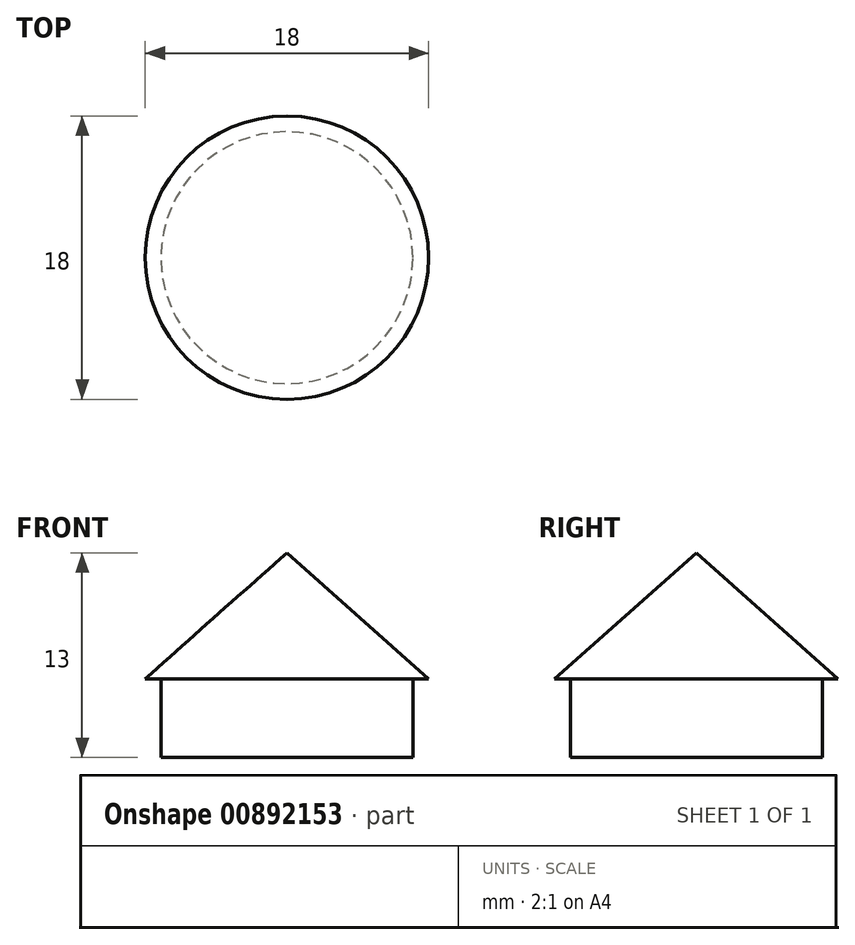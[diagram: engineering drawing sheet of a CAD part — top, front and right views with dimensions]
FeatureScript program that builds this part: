
annotation { "Feature Type Name" : "Feature", "Feature Type Description" : "" }
export const myFeature = defineFeature(function(context is Context, id is Id, definition is map)
    precondition{}
    {
        {
            var Q0;
            Q0=qCreatedBy(makeId("Top.planeOp"),FACE);
            var sketch = newSketch(context, id + "F0", { "sketchPlane" : qUnion([Q0])});
            skCircle(sketch, "E0", {"center": v(0, 0) * mm, "radius": 8 * mm});
            skSolve(sketch);
        }
        {
            var Q0;
            Q0 = qSketchRegion(id + "F0", true);
            extrude(context, id + "F1", {"entities" : qUnion([Q0]), "oppositeDirection" : true, "depth" : 5 * mm, "offsetDistance" : 25 * mm});
        }
        {
            var Q0;
            Q0=qCreatedBy(makeId("Right.planeOp"),FACE);
            var sketch = newSketch(context, id + "F2", { "sketchPlane" : qUnion([Q0])});
            skLineSegment(sketch, "E1", {"start": v(0, 0) * mm, "end": v(9, 0) * mm});
            skLineSegment(sketch, "E2", {"start": v(0, 0) * mm, "end": v(0, 8) * mm});
            skLineSegment(sketch, "E3", {"start": v(0, 8) * mm, "end": v(9, 0) * mm});
            skSolve(sketch);
        }
        {
            var Q0;
            Q0=makeQuery(id+"F2.imprint","IMPRINT",FACE,{"disambiguationData":[TD([[makeQuery(id+"F2.imprint","IMPRINT",EDGE,{"derivedFrom":sQuery(id+"F2.wireOp",EDGE,"E1")}),1.0]])]});
            var Q1;
            Q1=sQuery(id+"F2.wireOp",EDGE,"E2");
            revolve(context, id + "F3", {"operationType" : NewBodyOperationType.ADD, "surfaceOperationType" : NewSurfaceOperationType.NEW, "entities" : qUnion([Q0]), "axis" : qUnion([Q1]), "revolveType" : RevolveType.FULL});
        }
    });
